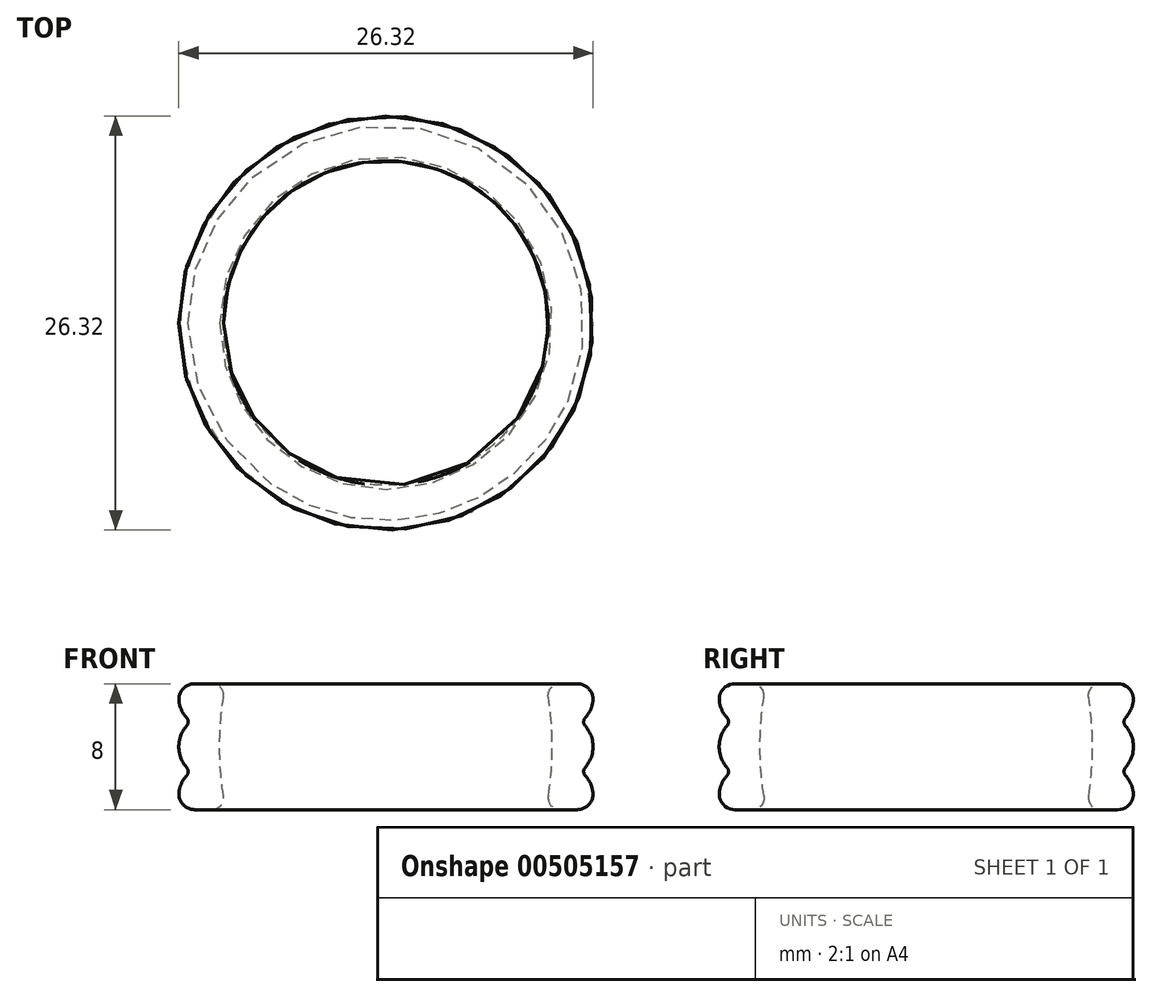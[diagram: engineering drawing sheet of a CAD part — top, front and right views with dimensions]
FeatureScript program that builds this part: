
annotation { "Feature Type Name" : "Feature", "Feature Type Description" : "" }
export const myFeature = defineFeature(function(context is Context, id is Id, definition is map)
    precondition{}
    {
        {
            var Q0;
            Q0=qCreatedBy(makeId("Front.planeOp"),FACE);
            var sketch = newSketch(context, id + "F0", { "sketchPlane" : qUnion([Q0])});
            skLineSegment(sketch, "E0", {"start": v(0, 0) * mm, "end": v(0, 7.56) * mm, "construction": true});
            skLineSegment(sketch, "E1", {"start": v(0, 0) * mm, "end": v(-35.38, 0) * mm, "construction": true});
            skLineSegment(sketch, "E2", {"start": v(-13.16, -4) * mm, "end": v(-13.16, 4) * mm, "construction": true});
            skLineSegment(sketch, "E3", {"start": v(-13.16, 4) * mm, "end": v(-10.16, 4) * mm, "construction": true});
            skLineSegment(sketch, "E4", {"start": v(-10.16, 4) * mm, "end": v(-10.16, 0) * mm, "construction": true});
            skLineSegment(sketch, "E5", {"start": v(-10.16, 0) * mm, "end": v(-10.16, -4) * mm, "construction": true});
            skLineSegment(sketch, "E6", {"start": v(-10.16, -4) * mm, "end": v(-13.16, -4) * mm, "construction": true});
            skArc(sketch, "E7", {"start": v(-10.31, 3.13) * mm, "mid": v(-10.56, 0) * mm, "end": v(-10.31, -3.13) * mm});
            skLineSegment(sketch, "E8", {"start": v(-11.06, 4) * mm, "end": v(-12.95, 4) * mm});
            skLineSegment(sketch, "E9", {"start": v(-12.95, -4) * mm, "end": v(-11.06, -4) * mm});
            skPoint(sketch, "E10.visualSharp", {"position": v(-10.16, 4) * mm});
            skArc(sketch, "E10.filletArc", {"start": v(-10.31, 3.13) * mm, "mid": v(-10.49, 3.74) * mm, "end": v(-11.06, 4) * mm});
            skPoint(sketch, "E11.visualSharp", {"position": v(-10.16, -4) * mm});
            skArc(sketch, "E11.filletArc", {"start": v(-11.06, -4) * mm, "mid": v(-10.49, -3.74) * mm, "end": v(-10.31, -3.13) * mm});
            skPoint(sketch, "E12.visualSharp", {"position": v(-13.16, -4) * mm});
            skPoint(sketch, "E13.visualSharp", {"position": v(-13.16, 4) * mm});
            skArc(sketch, "E14", {"start": v(-12.66, 1.31) * mm, "mid": v(-13.16, 0) * mm, "end": v(-12.66, -1.31) * mm});
            skArc(sketch, "E15", {"start": v(-12.66, 1.31) * mm, "mid": v(-12.56, 1.58) * mm, "end": v(-12.66, 1.85) * mm});
            skArc(sketch, "E16", {"start": v(-12.66, 1.85) * mm, "mid": v(-13.14, 2.88) * mm, "end": v(-12.95, 4) * mm});
            skArc(sketch, "E17", {"start": v(-12.66, -1.31) * mm, "mid": v(-12.56, -1.58) * mm, "end": v(-12.66, -1.85) * mm});
            skArc(sketch, "E18", {"start": v(-12.66, -1.85) * mm, "mid": v(-13.14, -2.88) * mm, "end": v(-12.95, -4) * mm});
            skLineSegment(sketch, "E19", {"start": v(-12.66, 1.31) * mm, "end": v(-12.66, -1.31) * mm, "construction": true});
            skSolve(sketch);
        }
        {
            var Q0;
            Q0=qSketchRegion(id+"F0",true);
            var Q1;
            Q1=sQuery(id+"F0.wireOp",EDGE,"E0");
            revolve(context, id + "F1", {"entities" : qUnion([Q0]), "axis" : qUnion([Q1]), "revolveType" : RevolveType.FULL});
        }
        {
            var Q0;
            Q0=makeQuery(id+"F1.opRevolve","SWEPT_EDGE",EDGE,{"disambiguationData":[OSD([sQuery(id+"F0.wireOp",EDGE,"E8"),sQuery(id+"F0.wireOp",EDGE,"E16")])]});
            var Q1;
            Q1=makeQuery(id+"F1.opRevolve","SWEPT_EDGE",EDGE,{"disambiguationData":[OSD([sQuery(id+"F0.wireOp",EDGE,"E9"),sQuery(id+"F0.wireOp",EDGE,"E18")])]});
            fillet(context, id + "F2", {"entities" : qUnion([Q0, Q1]), "radius" : 1 * mm, "tangentPropagation" : true, "allowEdgeOverflow" : false});
        }
    });
